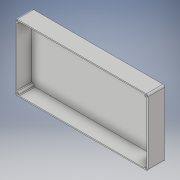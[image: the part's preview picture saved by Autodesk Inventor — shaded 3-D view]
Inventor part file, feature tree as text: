
AUTODESK INVENTOR PART (.ipt)
format: ipt  version: 2019.4 (Build 234330000, 330)  size: 200,704 bytes
history: native  units: mm
features: extrude x3, sketch x1
ambient origin geometry x8: Origin, YZ Plane, XZ Plane, XY Plane, X Axis, Y Axis, Z Axis, Center Point
bodies: Solid1 (feature_tree)
feature tree (4):
  sketch  "Sketch1"  dims[d0=300.0mm d1=150.0mm d2=295.0mm d3=145.0mm d4=4.0mm d5=4.0mm d6=4.0mm d7=4.0mm d8=4.0mm d9=4.0mm d10=4.0mm d11=4.0mm d12=4.0mm d13=4.0mm d14=4.0mm d15=4.0mm d16=5.0mm d17=5.0mm d18=5.0mm d19=5.0mm d20=4.0mm d21=4.0mm d22=4.0mm d23=4.0mm d24=4.0mm d25=4.0mm d26=4.0mm d27=4.0mm d28=4.0mm d29=4.0mm d30=4.0mm d31=4.0mm d32=1.5mm d33=1.5mm d34=1.5mm d35=1.5mm d36=1.5mm d37=1.5mm d38=1.5mm d39=1.5mm d40=1.5mm d41=1.5mm d42=1.5mm d43=1.5mm d44=1.5mm d45=1.5mm d46=1.5mm d47=1.5mm d48=1.5mm d49=1.5mm d50=1.5mm d51=1.5mm d52=1.5mm d53=1.5mm d54=1.5mm d55=1.5mm d56=2.5mm d57=0.0mm d58=37.5mm d59=0.0mm d60=35.5mm d61=0.0mm]
  extrude  "Extrusion1"  Depth=150.0mm
  extrude  "Extrusion2"  Depth=295.0mm
  extrude  "Extrusion3"  Depth=145.0mm
